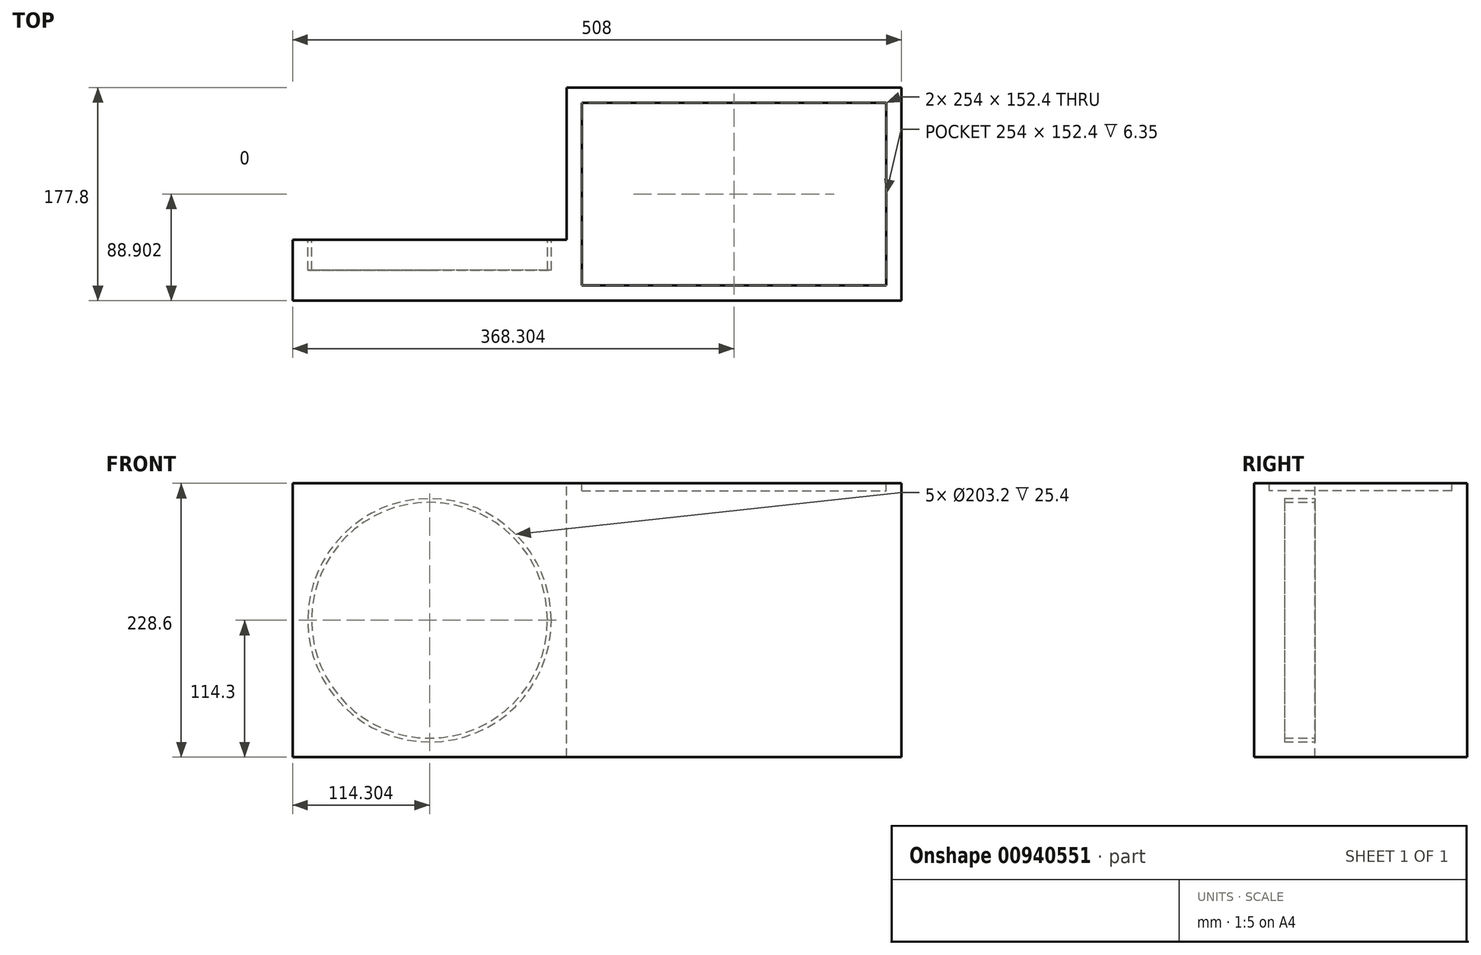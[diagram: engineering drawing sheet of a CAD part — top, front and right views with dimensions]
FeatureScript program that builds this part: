
annotation { "Feature Type Name" : "Feature", "Feature Type Description" : "" }
export const myFeature = defineFeature(function(context is Context, id is Id, definition is map)
    precondition{}
    {
        {
            var Q0;
            Q0=qCreatedBy(makeId("Top.planeOp"),FACE);
            var sketch = newSketch(context, id + "F0", { "sketchPlane" : qUnion([Q0])});
            skLineSegment(sketch, "E0", {"start": v(-21.58, 32.77) * mm, "end": v(257.82, 32.77) * mm});
            skLineSegment(sketch, "E1", {"start": v(257.82, 32.77) * mm, "end": v(257.82, -145.03) * mm});
            skLineSegment(sketch, "E2", {"start": v(257.82, -145.03) * mm, "end": v(-250.18, -145.03) * mm});
            skLineSegment(sketch, "E3", {"start": v(-250.18, -145.03) * mm, "end": v(-250.18, -94.23) * mm});
            skLineSegment(sketch, "E4", {"start": v(-21.58, -94.23) * mm, "end": v(-250.18, -94.23) * mm});
            skLineSegment(sketch, "E5.bottom", {"start": v(-8.88, 20.07) * mm, "end": v(245.12, 20.07) * mm});
            skLineSegment(sketch, "E5.top", {"start": v(-8.88, -132.33) * mm, "end": v(245.12, -132.33) * mm});
            skLineSegment(sketch, "E5.left", {"start": v(-8.88, 20.07) * mm, "end": v(-8.88, -132.33) * mm});
            skLineSegment(sketch, "E5.right", {"start": v(245.12, 20.07) * mm, "end": v(245.12, -132.33) * mm});
            skLineSegment(sketch, "E6", {"start": v(-21.58, 32.77) * mm, "end": v(-21.58, -94.23) * mm});
            skSolve(sketch);
        }
        {
            var Q0;
            Q0=makeQuery(id+"F0.imprint","IMPRINT",FACE,{"disambiguationData":[TD([[makeQuery(id+"F0.imprint","IMPRINT",EDGE,{"derivedFrom":sQuery(id+"F0.wireOp",EDGE,"E0")}),-1.0]])]});
            var Q1;
            Q1=makeQuery(id+"F0.imprint","IMPRINT",FACE,{"disambiguationData":[TD([[makeQuery(id+"F0.imprint","IMPRINT",EDGE,{"derivedFrom":sQuery(id+"F0.wireOp",EDGE,"E5.bottom")}),-1.0]])]});
            extrude(context, id + "F1", {"entities" : qUnion([Q0, Q1]), "oppositeDirection" : true, "depth" : 228.6 * mm, "offsetDistance" : 25.4 * mm});
        }
        {
            var Q0;
            Q0=makeQuery(id+"F0.imprint","IMPRINT",FACE,{"disambiguationData":[TD([[makeQuery(id+"F0.imprint","IMPRINT",EDGE,{"derivedFrom":sQuery(id+"F0.wireOp",EDGE,"E5.bottom")}),-1.0]])]});
            extrude(context, id + "F2", {"entities" : qUnion([Q0]), "operationType" : NewBodyOperationType.REMOVE, "oppositeDirection" : true, "depth" : 6.35 * mm, "offsetDistance" : 25.4 * mm});
        }
        {
            var Q0;
            Q0=makeQuery(id+"F1.opExtrude","SWEPT_FACE",FACE,{"disambiguationData":[OSD([sQuery(id+"F0.wireOp",EDGE,"E4")])]});
            var sketch = newSketch(context, id + "F3", { "sketchPlane" : qUnion([Q0])});
            skLineSegment(sketch, "E7", {"start": v(21.58, 0) * mm, "end": v(135.88, 0) * mm});
            skLineSegment(sketch, "E8", {"start": v(135.88, 0) * mm, "end": v(135.88, -114.3) * mm});
            skCircle(sketch, "E9", {"center": v(135.88, -114.3) * mm, "radius": 101.6 * mm});
            skCircle(sketch, "E10", {"center": v(135.88, -114.3) * mm, "radius": 98.43 * mm});
            skSolve(sketch);
        }
        {
            var Q0;
            Q0=makeQuery(id+"F3.imprint","IMPRINT",FACE,{"disambiguationData":[TD([[makeQuery(id+"F3.imprint","IMPRINT",EDGE,{"derivedFrom":sQuery(id+"F3.wireOp",EDGE,"E9")}),1.0]])]});
            extrude(context, id + "F4", {"entities" : qUnion([Q0]), "operationType" : NewBodyOperationType.REMOVE, "oppositeDirection" : true, "depth" : 25.4 * mm, "offsetDistance" : 25.4 * mm});
        }
    });
